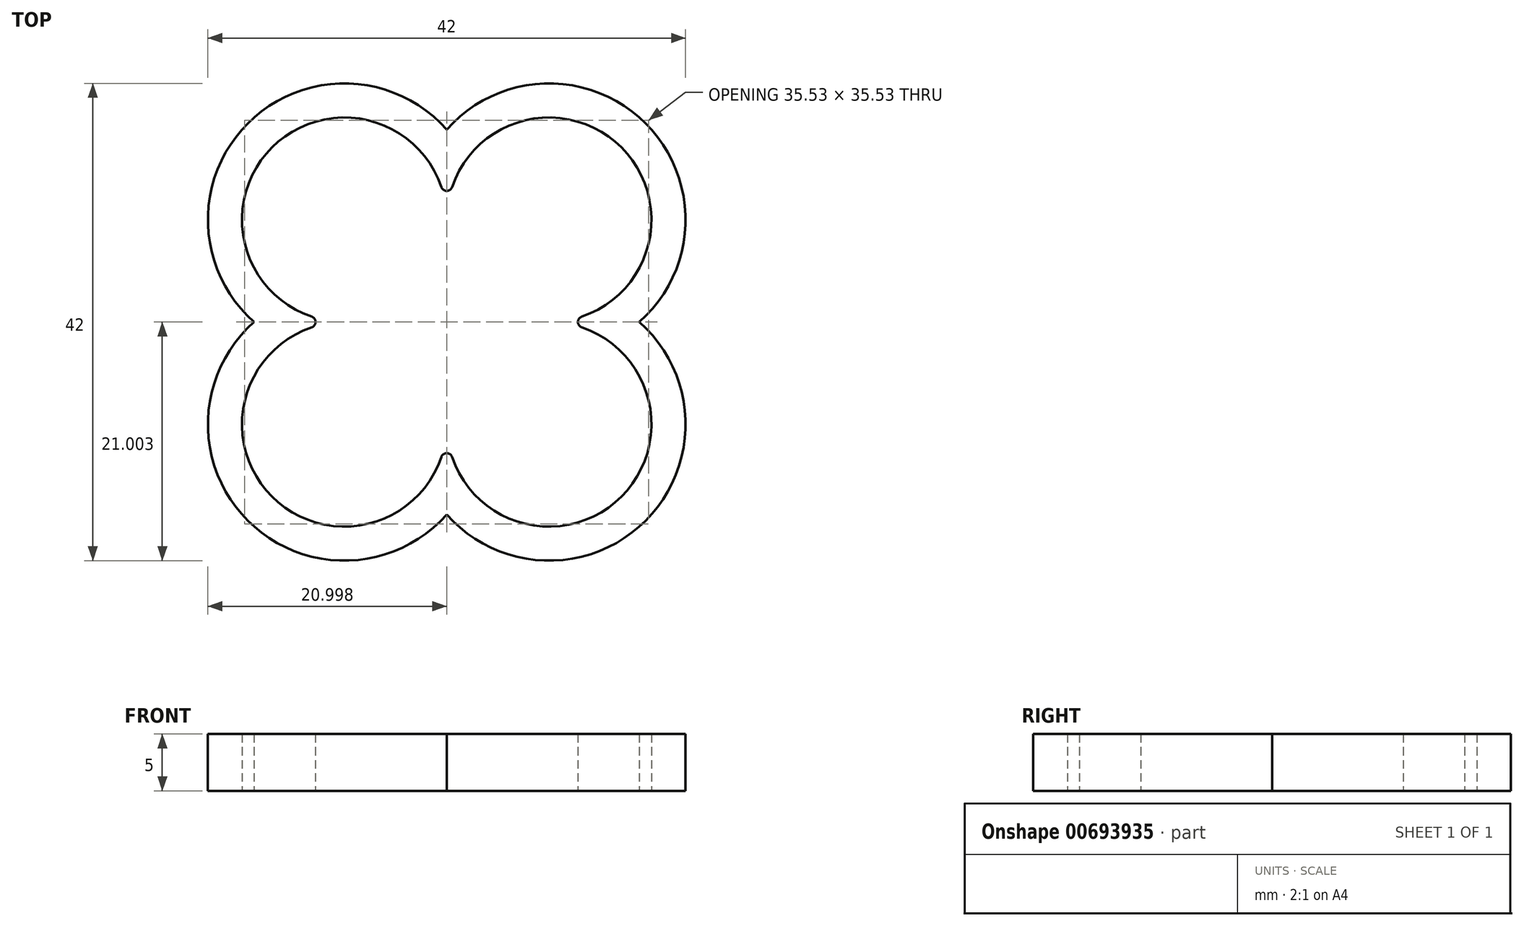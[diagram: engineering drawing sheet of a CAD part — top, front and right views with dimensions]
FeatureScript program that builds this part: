
annotation { "Feature Type Name" : "Feature", "Feature Type Description" : "" }
export const myFeature = defineFeature(function(context is Context, id is Id, definition is map)
    precondition{}
    {
        {
            var Q0;
            Q0=qCreatedBy(makeId("Top.planeOp"),FACE);
            var sketch = newSketch(context, id + "F0", { "sketchPlane" : qUnion([Q0])});
            skArc(sketch, "E0", {"start": v(-21.96, 31.54) * mm, "mid": v(-25.45, 16.65) * mm, "end": v(-10.56, 20.13) * mm});
            skArc(sketch, "E1.0.1.0", {"start": v(-10.56, 43.9) * mm, "mid": v(-25.45, 47.38) * mm, "end": v(-21.96, 32.49) * mm});
            skArc(sketch, "E1.1.0.0", {"start": v(-9.6, 20.13) * mm, "mid": v(5.28, 16.65) * mm, "end": v(1.8, 31.54) * mm});
            skArc(sketch, "E1.1.1.0", {"start": v(1.8, 32.49) * mm, "mid": v(5.28, 47.38) * mm, "end": v(-9.6, 43.9) * mm});
            skLineSegment(sketch, "E1.direction1", {"start": v(-19.08, 23.01) * mm, "end": v(-1.08, 23.01) * mm, "construction": true});
            skLineSegment(sketch, "E1.direction2", {"start": v(-19.08, 23.01) * mm, "end": v(-19.08, 41.01) * mm, "construction": true});
            skPoint(sketch, "E2.visualSharp", {"position": v(-10.08, 41.01) * mm});
            skArc(sketch, "E2.filletArc", {"start": v(-10.56, 43.9) * mm, "mid": v(-10.08, 43.55) * mm, "end": v(-9.6, 43.9) * mm});
            skPoint(sketch, "E3.visualSharp", {"position": v(-1.08, 32.01) * mm});
            skArc(sketch, "E3.filletArc", {"start": v(1.8, 32.49) * mm, "mid": v(1.46, 32.01) * mm, "end": v(1.8, 31.54) * mm});
            skPoint(sketch, "E4.visualSharp", {"position": v(-10.08, 23.01) * mm});
            skArc(sketch, "E4.filletArc", {"start": v(-9.6, 20.13) * mm, "mid": v(-10.08, 20.47) * mm, "end": v(-10.56, 20.13) * mm});
            skPoint(sketch, "E5.visualSharp", {"position": v(-19.08, 32.01) * mm});
            skArc(sketch, "E5.filletArc", {"start": v(-21.96, 31.54) * mm, "mid": v(-21.62, 32.01) * mm, "end": v(-21.96, 32.49) * mm});
            skArc(sketch, "E6.0", {"start": v(-10.08, 48.95) * mm, "mid": v(-27.57, 49.5) * mm, "end": v(-27.02, 32.01) * mm});
            skArc(sketch, "E6.1", {"start": v(6.86, 32.01) * mm, "mid": v(7.4, 49.5) * mm, "end": v(-10.08, 48.95) * mm});
            skArc(sketch, "E6.2", {"start": v(-10.08, 15.08) * mm, "mid": v(7.4, 14.53) * mm, "end": v(6.86, 32.01) * mm});
            skArc(sketch, "E6.3", {"start": v(-27.02, 32.01) * mm, "mid": v(-27.57, 14.53) * mm, "end": v(-10.08, 15.08) * mm});
            skSolve(sketch);
        }
        {
            var Q0;
            Q0=makeQuery(id+"F0.imprint","IMPRINT",FACE,{"disambiguationData":[TD([[makeQuery(id+"F0.imprint","IMPRINT",EDGE,{"derivedFrom":sQuery(id+"F0.wireOp",EDGE,"E0")}),-1.0]])]});
            extrude(context, id + "F1", {"entities" : qUnion([Q0]), "depth" : 5 * mm, "offsetDistance" : 25 * mm});
        }
    });
